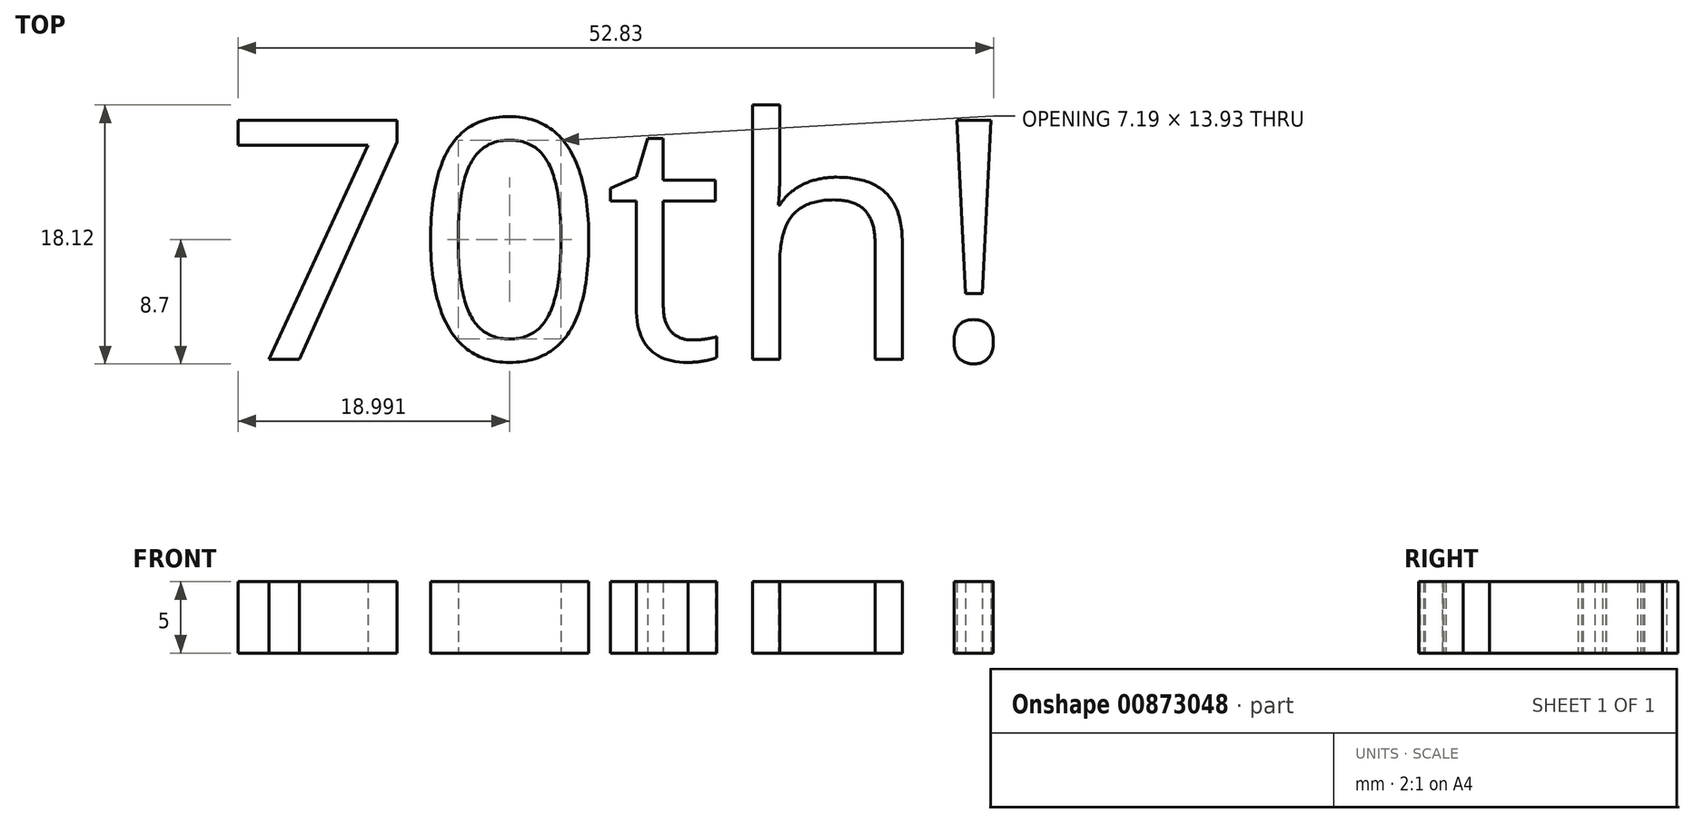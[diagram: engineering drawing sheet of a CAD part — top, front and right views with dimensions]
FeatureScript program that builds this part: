
annotation { "Feature Type Name" : "Feature", "Feature Type Description" : "" }
export const myFeature = defineFeature(function(context is Context, id is Id, definition is map)
    precondition{}
    {
        {
            var Q0;
            Q0=qCreatedBy(makeId("Top.planeOp"),FACE);
            var sketch = newSketch(context, id + "F0", { "sketchPlane" : qUnion([Q0])});
            skText(sketch, "E0", { "text": "70th!", "fontName": "OpenSans-Regular.ttf"});
            const initialGuessF0  = {"E0": [-0.00743, -0.01057, 1, 0, 0.01686]};
            skSetInitialGuess(sketch, initialGuessF0);
            skSolve(sketch);
        }
        {
            var Q0;
            Q0 = qSketchRegion(id + "F0", true);
            extrude(context, id + "F1", {"entities" : qUnion([Q0]), "depth" : 5 * mm, "offsetDistance" : 25 * mm});
        }
    });
